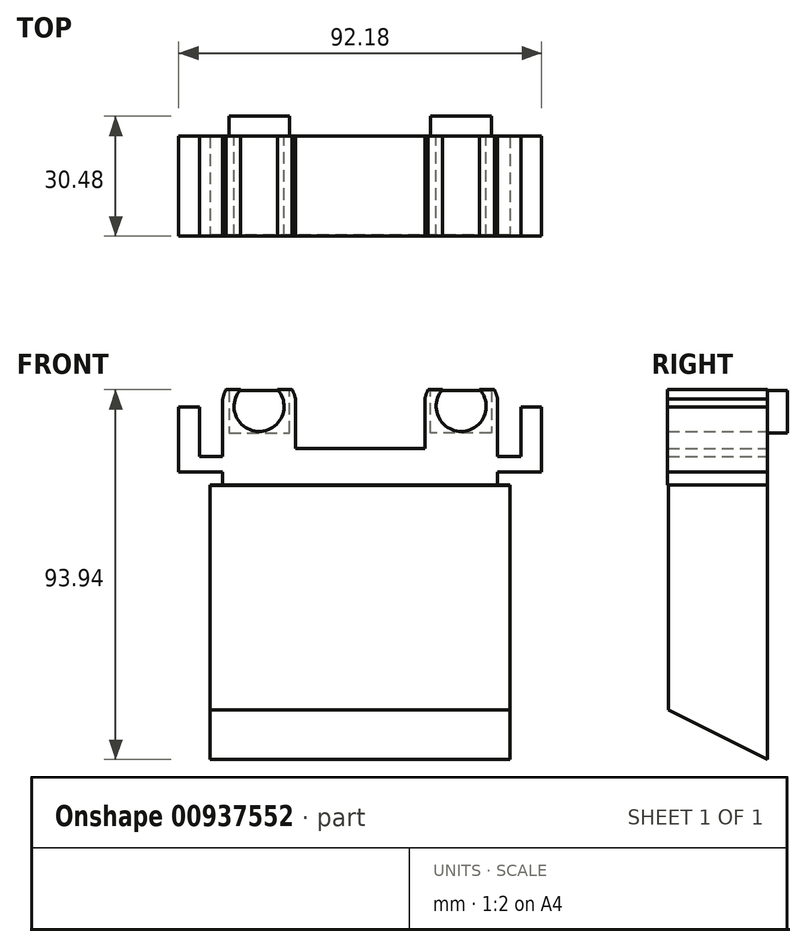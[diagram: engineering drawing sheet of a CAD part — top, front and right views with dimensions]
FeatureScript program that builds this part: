
annotation { "Feature Type Name" : "Feature", "Feature Type Description" : "" }
export const myFeature = defineFeature(function(context is Context, id is Id, definition is map)
    precondition{}
    {
        {
            var Q0;
            Q0=qCreatedBy(makeId("Front.planeOp"),FACE);
            var sketch = newSketch(context, id + "F0", { "sketchPlane" : qUnion([Q0])});
            skLineSegment(sketch, "E0", {"start": v(-34.9, 12.57) * mm, "end": v(-34.9, -9.28) * mm});
            skLineSegment(sketch, "E1", {"start": v(-34.9, -9.28) * mm, "end": v(0, -9.28) * mm});
            skLineSegment(sketch, "E2", {"start": v(0, -9.28) * mm, "end": v(0, 0) * mm, "construction": true});
            skLineSegment(sketch, "E3", {"start": v(0, 0) * mm, "end": v(-16.44, 0) * mm});
            skLineSegment(sketch, "E4", {"start": v(-16.44, 0) * mm, "end": v(-16.44, 12.57) * mm});
            skLineSegment(sketch, "E5.MirrorCS", {"start": v(0, 0) * mm, "end": v(16.44, 0) * mm});
            skLineSegment(sketch, "E6.MirrorCS", {"start": v(34.9, -9.28) * mm, "end": v(0, -9.28) * mm});
            skLineSegment(sketch, "E7.MirrorCS", {"start": v(34.9, 12.57) * mm, "end": v(34.9, -9.28) * mm});
            skLineSegment(sketch, "E8.MirrorCS", {"start": v(16.44, 0) * mm, "end": v(16.44, 12.57) * mm});
            skPoint(sketch, "E9.centerSnap0", {"position": v(25.67, 4.32) * mm});
            skCircle(sketch, "E10", {"center": v(-25.67, 10.67) * mm, "radius": 6.35 * mm});
            skCircle(sketch, "E11", {"center": v(25.67, 10.67) * mm, "radius": 6.35 * mm});
            skArc(sketch, "E12", {"start": v(-16.44, 12.57) * mm, "mid": v(-25.67, 20.1) * mm, "end": v(-34.9, 12.57) * mm});
            skArc(sketch, "E13", {"start": v(34.9, 12.57) * mm, "mid": v(25.67, 20.1) * mm, "end": v(16.44, 12.57) * mm});
            skSolve(sketch);
        }
        {
            var Q0;
            Q0=qSketchRegion(id+"F0",true);
            extrude(context, id + "F1", {"entities" : qUnion([Q0]), "depth" : 25.4 * mm, "offsetDistance" : 25.4 * mm});
        }
        {
            var Q0;
            Q0=qCreatedBy(makeId("Right.planeOp"),FACE);
            var sketch = newSketch(context, id + "F2", { "sketchPlane" : qUnion([Q0])});
            skLineSegment(sketch, "E14", {"start": v(-25.4, -9.27) * mm, "end": v(0, -22.67) * mm});
            skLineSegment(sketch, "E15", {"start": v(0, -22.67) * mm, "end": v(0, -9.27) * mm});
            skLineSegment(sketch, "E16", {"start": v(0, -9.27) * mm, "end": v(-25.4, -9.27) * mm});
            skSolve(sketch);
        }
        {
            var Q0;
            Q0=qSketchRegion(id+"F2",true);
            extrude(context, id + "F3", {"entities" : qUnion([Q0]), "operationType" : NewBodyOperationType.ADD, "depth" : 38.1 * mm, "offsetDistance" : 25.4 * mm, "hasSecondDirection" : true, "secondDirectionOppositeDirection" : true, "secondDirectionDepth" : 38.1 * mm});
        }
        {
            var Q0;
            Q0=qCreatedBy(makeId("Right.planeOp"),FACE);
            var sketch = newSketch(context, id + "F4", { "sketchPlane" : qUnion([Q0])});
            skLineSegment(sketch, "E17", {"start": v(0, -21.85) * mm, "end": v(0, -79) * mm});
            skLineSegment(sketch, "E18", {"start": v(0, -79) * mm, "end": v(0, -21.85) * mm});
            skPoint(sketch, "E19.orphan", {"position": v(0, 20.56) * mm});
            skLineSegment(sketch, "E20", {"start": v(0, -21.85) * mm, "end": v(-25.16, -9.3) * mm});
            skLineSegment(sketch, "E21", {"start": v(-25.16, -9.3) * mm, "end": v(-25.16, -66.46) * mm});
            skLineSegment(sketch, "E22", {"start": v(0, -79) * mm, "end": v(-25.16, -66.46) * mm});
            skSolve(sketch);
        }
        {
            var Q0;
            Q0 = qSketchRegion(id + "F4", true);
            extrude(context, id + "F5", {"entities" : qUnion([Q0]), "operationType" : NewBodyOperationType.ADD, "depth" : 38.1 * mm, "offsetDistance" : 25.4 * mm, "hasSecondDirection" : true, "secondDirectionOppositeDirection" : true, "secondDirectionDepth" : 38.1 * mm});
        }
        {
            var Q0;
            Q0=qCreatedBy(makeId("Front.planeOp"),FACE);
            var sketch = newSketch(context, id + "F6", { "sketchPlane" : qUnion([Q0])});
            skLineSegment(sketch, "E23", {"start": v(-34.64, -6) * mm, "end": v(-46.09, -6) * mm});
            skLineSegment(sketch, "E24", {"start": v(-46.09, -6) * mm, "end": v(-46.09, 10.52) * mm});
            skLineSegment(sketch, "E25", {"start": v(-46.09, 10.52) * mm, "end": v(-40.83, 10.52) * mm});
            skLineSegment(sketch, "E26", {"start": v(-40.83, 10.52) * mm, "end": v(-40.83, -2.06) * mm});
            skLineSegment(sketch, "E27", {"start": v(-40.83, -2.06) * mm, "end": v(-34.83, -2.06) * mm});
            skLineSegment(sketch, "E28", {"start": v(-34.83, -2.06) * mm, "end": v(-34.64, -6) * mm});
            skLineSegment(sketch, "E29.MirrorCS", {"start": v(40.83, -2.06) * mm, "end": v(34.83, -2.06) * mm});
            skLineSegment(sketch, "E30.MirrorCS", {"start": v(34.83, -2.06) * mm, "end": v(34.64, -6) * mm});
            skLineSegment(sketch, "E31.MirrorCS", {"start": v(34.64, -6) * mm, "end": v(46.09, -6) * mm});
            skLineSegment(sketch, "E32.MirrorCS", {"start": v(46.09, -6) * mm, "end": v(46.09, 10.52) * mm});
            skLineSegment(sketch, "E33.MirrorCS", {"start": v(40.83, 10.52) * mm, "end": v(40.83, -2.06) * mm});
            skLineSegment(sketch, "E34.MirrorCS", {"start": v(46.09, 10.52) * mm, "end": v(40.83, 10.52) * mm});
            skSolve(sketch);
        }
        {
            var Q0;
            Q0 = qSketchRegion(id + "F6", true);
            extrude(context, id + "F7", {"entities" : qUnion([Q0]), "operationType" : NewBodyOperationType.ADD, "depth" : 25.4 * mm, "offsetDistance" : 25.4 * mm});
        }
        {
            var Q0;
            Q0=qCreatedBy(makeId("Front.planeOp"),FACE);
            var sketch = newSketch(context, id + "F8", { "sketchPlane" : qUnion([Q0])});
            skLineSegment(sketch, "E35", {"start": v(-55.07, 14.94) * mm, "end": v(55.07, 14.94) * mm});
            skLineSegment(sketch, "E36", {"start": v(55.07, 14.94) * mm, "end": v(55.07, 32.9) * mm});
            skLineSegment(sketch, "E37", {"start": v(55.07, 32.9) * mm, "end": v(-55.07, 32.9) * mm});
            skLineSegment(sketch, "E38", {"start": v(-55.07, 32.9) * mm, "end": v(-55.07, 14.94) * mm});
            skLineSegment(sketch, "E39", {"start": v(0, 0) * mm, "end": v(0, 14.94) * mm, "construction": true});
            skSolve(sketch);
        }
        {
            var Q0;
            Q0=makeQuery(id+"F8.imprint","IMPRINT",FACE,{"disambiguationData":[TD([[makeQuery(id+"F8.imprint","IMPRINT",EDGE,{"derivedFrom":sQuery(id+"F8.wireOp",EDGE,"E35")}),1.0]])]});
            extrude(context, id + "F9", {"entities" : qUnion([Q0]), "operationType" : NewBodyOperationType.REMOVE, "depth" : 25.4 * mm, "offsetDistance" : 25.4 * mm});
        }
        {
            var Q0;
            Q0=qCreatedBy(makeId("Front.planeOp"),FACE);
            var sketch = newSketch(context, id + "F10", { "sketchPlane" : qUnion([Q0])});
            skLineSegment(sketch, "E40", {"start": v(33.31, 3.97) * mm, "end": v(17.92, 3.97) * mm});
            skLineSegment(sketch, "E41", {"start": v(17.92, 3.97) * mm, "end": v(17.92, 14.77) * mm});
            skLineSegment(sketch, "E42", {"start": v(17.92, 14.77) * mm, "end": v(33.31, 14.77) * mm});
            skLineSegment(sketch, "E43", {"start": v(33.31, 14.77) * mm, "end": v(33.31, 3.97) * mm});
            skLineSegment(sketch, "E44.MirrorCS", {"start": v(-17.92, 14.77) * mm, "end": v(-33.31, 14.77) * mm});
            skLineSegment(sketch, "E45.MirrorCS", {"start": v(-17.92, 3.97) * mm, "end": v(-17.92, 14.77) * mm});
            skLineSegment(sketch, "E46.MirrorCS", {"start": v(-33.31, 3.97) * mm, "end": v(-17.92, 3.97) * mm});
            skLineSegment(sketch, "E47.MirrorCS", {"start": v(-33.31, 14.77) * mm, "end": v(-33.31, 3.97) * mm});
            skSolve(sketch);
        }
        {
            var Q0;
            Q0 = qSketchRegion(id + "F10", true);
            extrude(context, id + "F11", {"entities" : qUnion([Q0]), "operationType" : NewBodyOperationType.ADD, "depth" : 0 * mm, "offsetDistance" : 25.4 * mm, "hasSecondDirection" : true, "secondDirectionOppositeDirection" : true, "secondDirectionDepth" : 5.08 * mm});
        }
    });
